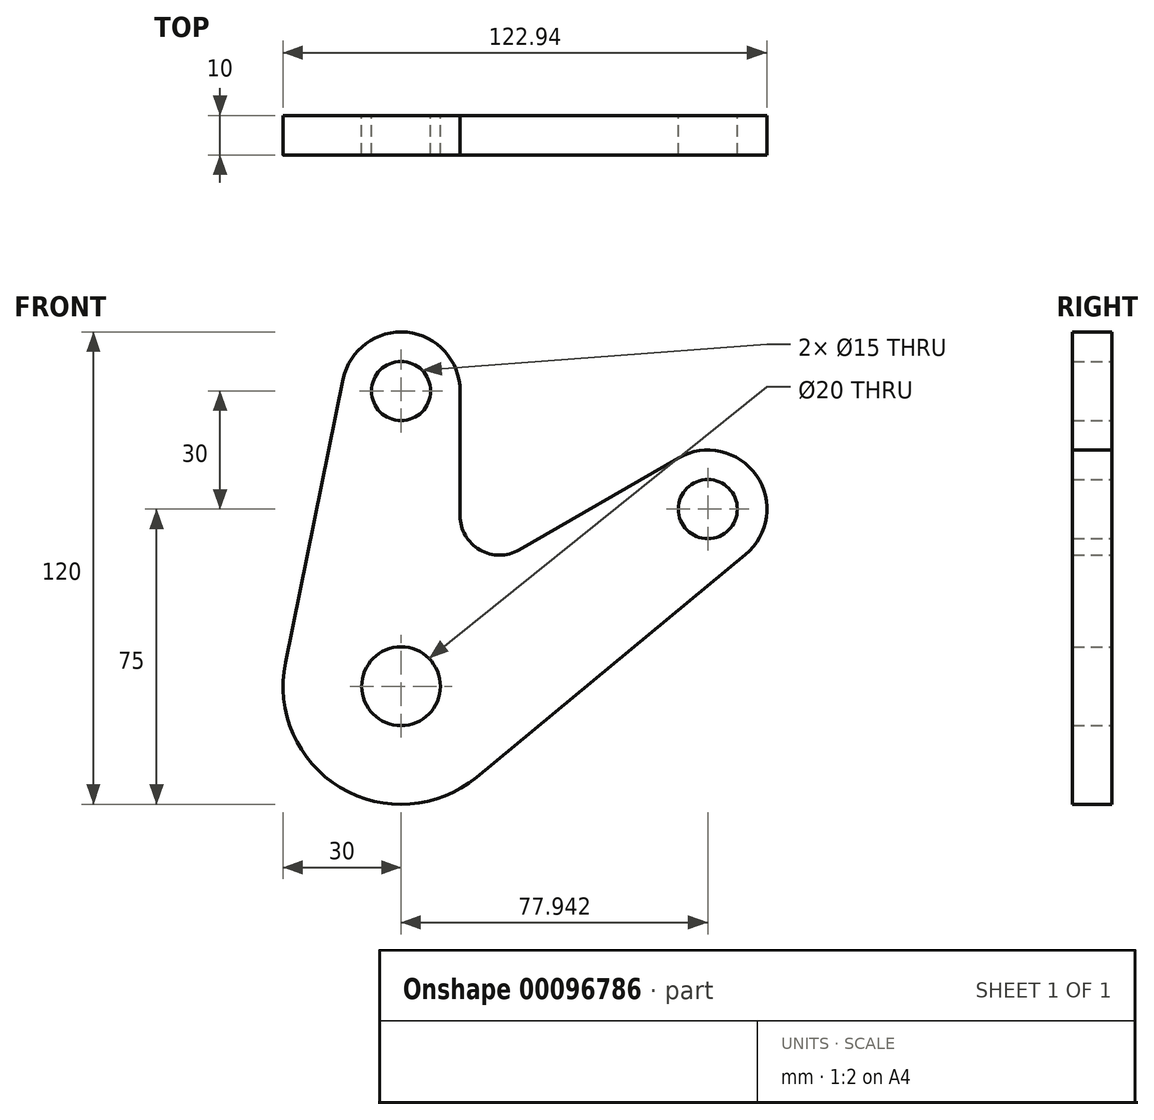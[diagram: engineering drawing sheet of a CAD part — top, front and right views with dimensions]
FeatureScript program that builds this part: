
annotation { "Feature Type Name" : "Feature", "Feature Type Description" : "" }
export const myFeature = defineFeature(function(context is Context, id is Id, definition is map)
    precondition{}
    {
        {
            var Q0;
            Q0=qCreatedBy(makeId("Front.planeOp"),FACE);
            var sketch = newSketch(context, id + "F0", { "sketchPlane" : qUnion([Q0])});
            skLineSegment(sketch, "E0", {"start": v(0, 90) * mm, "end": v(0, -17.65) * mm, "construction": true});
            skLineSegment(sketch, "E1", {"start": v(-13.23, 0) * mm, "end": v(12.25, 0) * mm, "construction": true});
            skLineSegment(sketch, "E2", {"start": v(0, 0) * mm, "end": v(77.94, 45) * mm, "construction": true});
            skCircle(sketch, "E3", {"center": v(0, 0) * mm, "radius": 10 * mm});
            skCircle(sketch, "E4", {"center": v(0, 75) * mm, "radius": 7.5 * mm});
            skCircle(sketch, "E5", {"center": v(77.94, 45) * mm, "radius": 7.5 * mm});
            skLineSegment(sketch, "E6", {"start": v(15, 75) * mm, "end": v(15, 43.3) * mm});
            skLineSegment(sketch, "E7", {"start": v(70.44, 58) * mm, "end": v(30, 34.64) * mm});
            skArc(sketch, "E8", {"start": v(15, 43.3) * mm, "mid": v(20, 34.64) * mm, "end": v(30, 34.64) * mm});
            skLineSegment(sketch, "E9", {"start": v(-14.7, 78) * mm, "end": v(-29.4, 6) * mm});
            skArc(sketch, "E10", {"start": v(-14.7, 78) * mm, "mid": v(1.5, 89.92) * mm, "end": v(15, 75) * mm});
            skArc(sketch, "E11", {"start": v(70.44, 58) * mm, "mid": v(90.26, 53.56) * mm, "end": v(87.5, 33.44) * mm});
            skArc(sketch, "E12", {"start": v(-29.4, 6) * mm, "mid": v(-15.44, -25.72) * mm, "end": v(19.12, -23.12) * mm});
            skLineSegment(sketch, "E13", {"start": v(87.5, 33.44) * mm, "end": v(19.12, -23.12) * mm});
            skSolve(sketch);
        }
        {
            var Q0;
            Q0 = qSketchRegion(id + "F0", true);
            extrude(context, id + "F1", {"entities" : qUnion([Q0]), "depth" : 10 * mm});
        }
    });
